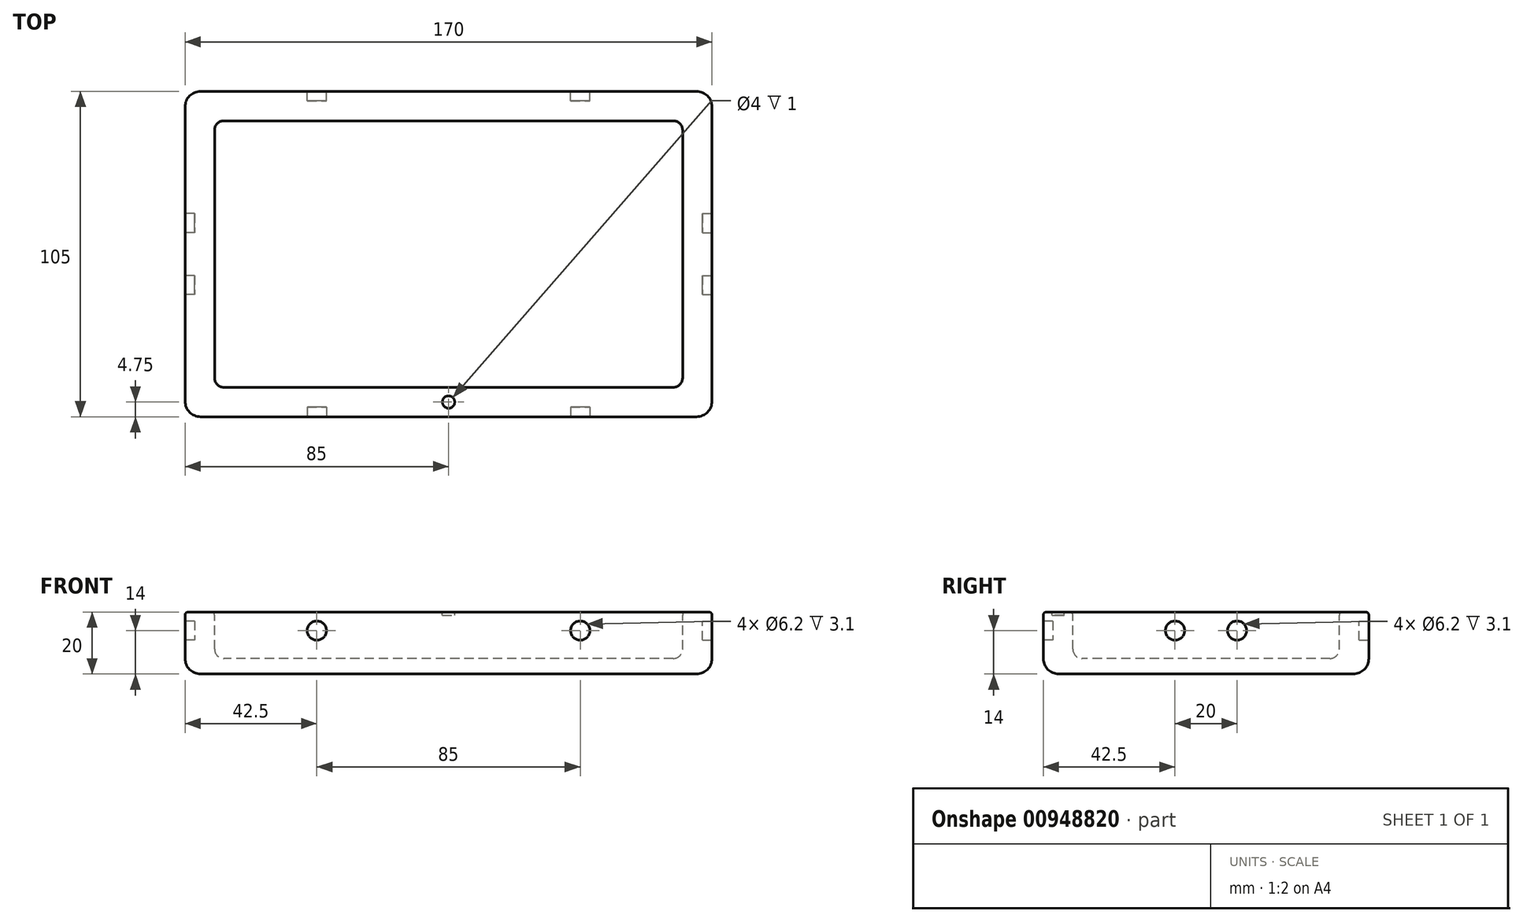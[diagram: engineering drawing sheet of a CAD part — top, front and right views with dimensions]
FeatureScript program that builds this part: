
annotation { "Feature Type Name" : "Feature", "Feature Type Description" : "" }
export const myFeature = defineFeature(function(context is Context, id is Id, definition is map)
    precondition{}
    {
        {
            var Q0;
            Q0=qCreatedBy(makeId("Top.planeOp"),FACE);
            var sketch = newSketch(context, id + "F0", { "sketchPlane" : qUnion([Q0])});
            skLineSegment(sketch, "E0.bottom", {"start": v(-85, 52.5) * mm, "end": v(85, 52.5) * mm});
            skLineSegment(sketch, "E0.top", {"start": v(-85, -52.5) * mm, "end": v(85, -52.5) * mm});
            skLineSegment(sketch, "E0.left", {"start": v(-85, 52.5) * mm, "end": v(-85, -52.5) * mm});
            skLineSegment(sketch, "E0.right", {"start": v(85, 52.5) * mm, "end": v(85, -52.5) * mm});
            skLineSegment(sketch, "E1.bottom", {"start": v(-72.5, 43) * mm, "end": v(72.5, 43) * mm});
            skLineSegment(sketch, "E1.top", {"start": v(-72.5, -43) * mm, "end": v(72.5, -43) * mm});
            skLineSegment(sketch, "E1.left", {"start": v(-75.5, 40) * mm, "end": v(-75.5, -40) * mm});
            skLineSegment(sketch, "E1.right", {"start": v(75.5, 40) * mm, "end": v(75.5, -40) * mm});
            skLineSegment(sketch, "E2.direction1", {"start": v(-75.5, -43) * mm, "end": v(15.26, -43) * mm, "construction": true});
            skPoint(sketch, "E3.visualSharp", {"position": v(-75.5, 43) * mm});
            skArc(sketch, "E3.filletArc", {"start": v(-72.5, 43) * mm, "mid": v(-74.62, 42.12) * mm, "end": v(-75.5, 40) * mm});
            skPoint(sketch, "E4.visualSharp", {"position": v(75.5, 43) * mm});
            skArc(sketch, "E4.filletArc", {"start": v(75.5, 40) * mm, "mid": v(74.62, 42.12) * mm, "end": v(72.5, 43) * mm});
            skPoint(sketch, "E5.visualSharp", {"position": v(75.5, -43) * mm});
            skArc(sketch, "E5.filletArc", {"start": v(72.5, -43) * mm, "mid": v(74.62, -42.12) * mm, "end": v(75.5, -40) * mm});
            skPoint(sketch, "E6.visualSharp", {"position": v(-75.5, -43) * mm});
            skArc(sketch, "E6.filletArc", {"start": v(-75.5, -40) * mm, "mid": v(-74.62, -42.12) * mm, "end": v(-72.5, -43) * mm});
            skLineSegment(sketch, "E7.direction1", {"start": v(-75.5, -43) * mm, "end": v(17, -43) * mm, "construction": true});
            skLineSegment(sketch, "E8", {"start": v(-85, 0) * mm, "end": v(85, 0) * mm, "construction": true});
            skLineSegment(sketch, "E9", {"start": v(0, -52.5) * mm, "end": v(0, 52.5) * mm, "construction": true});
            skCircle(sketch, "E10", {"center": v(0, -47.75) * mm, "radius": 2 * mm});
            skSolve(sketch);
        }
        {
            var Q0;
            Q0=makeQuery(id+"F0.imprint","IMPRINT",FACE,{"disambiguationData":[TD([[makeQuery(id+"F0.imprint","IMPRINT",EDGE,{"derivedFrom":sQuery(id+"F0.wireOp",EDGE,"E1.bottom")}),-1.0]])]});
            var Q1;
            Q1=makeQuery(id+"F0.imprint","IMPRINT",FACE,{"disambiguationData":[TD([[makeQuery(id+"F0.imprint","IMPRINT",EDGE,{"derivedFrom":sQuery(id+"F0.wireOp",EDGE,"E0.bottom")}),-1.0]])]});
            var Q2;
            Q2=makeQuery(id+"F0.imprint","IMPRINT",FACE,{"disambiguationData":[TD([[makeQuery(id+"F0.imprint","IMPRINT",EDGE,{"derivedFrom":sQuery(id+"F0.wireOp",EDGE,"E2.0.2.0")}),1.0]])]});
            var Q3;
            Q3=makeQuery(id+"F0.imprint","IMPRINT",FACE,{"disambiguationData":[TD([[makeQuery(id+"F0.imprint","IMPRINT",EDGE,{"derivedFrom":sQuery(id+"F0.wireOp",EDGE,"E2.0.3.0")}),1.0]])]});
            var Q4;
            Q4=makeQuery(id+"F0.imprint","IMPRINT",FACE,{"disambiguationData":[TD([[makeQuery(id+"F0.imprint","IMPRINT",EDGE,{"derivedFrom":sQuery(id+"F0.wireOp",EDGE,"E2.0.1.0")}),1.0]])]});
            var Q5;
            Q5=makeQuery(id+"F0.imprint","IMPRINT",FACE,{"disambiguationData":[TD([[makeQuery(id+"F0.imprint","IMPRINT",EDGE,{"derivedFrom":sQuery(id+"F0.wireOp",EDGE,"E7.0.1.2")}),1.0]])]});
            var Q6;
            Q6=makeQuery(id+"F0.imprint","IMPRINT",FACE,{"disambiguationData":[TD([[makeQuery(id+"F0.imprint","IMPRINT",EDGE,{"derivedFrom":sQuery(id+"F0.wireOp",EDGE,"E7.0.2.2")}),1.0]])]});
            var Q7;
            Q7=makeQuery(id+"F0.imprint","IMPRINT",FACE,{"disambiguationData":[TD([[makeQuery(id+"F0.imprint","IMPRINT",EDGE,{"derivedFrom":sQuery(id+"F0.wireOp",EDGE,"E7.0.3.2")}),1.0]])]});
            var Q8;
            Q8=makeQuery(id+"F0.imprint","IMPRINT",FACE,{"disambiguationData":[TD([[makeQuery(id+"F0.imprint","IMPRINT",EDGE,{"derivedFrom":sQuery(id+"F0.wireOp",EDGE,"E10")}),1.0]])]});
            extrude(context, id + "F1", {"entities" : qUnion([Q0, Q1, Q2, Q3, Q4, Q5, Q6, Q7, Q8]), "depth" : 20 * mm, "offsetDistance" : 25 * mm});
        }
        {
            var Q0;
            Q0=makeQuery(id+"F0.imprint","IMPRINT",FACE,{"disambiguationData":[TD([[makeQuery(id+"F0.imprint","IMPRINT",EDGE,{"derivedFrom":sQuery(id+"F0.wireOp",EDGE,"E1.bottom")}),-1.0]])]});
            var Q1;
            Q1=makeQuery(id+"F0.imprint","IMPRINT",FACE,{"disambiguationData":[TD([[makeQuery(id+"F0.imprint","IMPRINT",EDGE,{"derivedFrom":sQuery(id+"F0.wireOp",EDGE,"E2.0.1.0")}),1.0]])]});
            var Q2;
            Q2=makeQuery(id+"F0.imprint","IMPRINT",FACE,{"disambiguationData":[TD([[makeQuery(id+"F0.imprint","IMPRINT",EDGE,{"derivedFrom":sQuery(id+"F0.wireOp",EDGE,"E2.0.2.0")}),1.0]])]});
            var Q3;
            Q3=makeQuery(id+"F0.imprint","IMPRINT",FACE,{"disambiguationData":[TD([[makeQuery(id+"F0.imprint","IMPRINT",EDGE,{"derivedFrom":sQuery(id+"F0.wireOp",EDGE,"E2.0.3.0")}),1.0]])]});
            var Q4;
            Q4=makeQuery(id+"F0.imprint","IMPRINT",FACE,{"disambiguationData":[TD([[makeQuery(id+"F0.imprint","IMPRINT",EDGE,{"derivedFrom":sQuery(id+"F0.wireOp",EDGE,"E7.0.1.2")}),1.0]])]});
            var Q5;
            Q5=makeQuery(id+"F0.imprint","IMPRINT",FACE,{"disambiguationData":[TD([[makeQuery(id+"F0.imprint","IMPRINT",EDGE,{"derivedFrom":sQuery(id+"F0.wireOp",EDGE,"E7.0.2.2")}),1.0]])]});
            var Q6;
            Q6=makeQuery(id+"F0.imprint","IMPRINT",FACE,{"disambiguationData":[TD([[makeQuery(id+"F0.imprint","IMPRINT",EDGE,{"derivedFrom":sQuery(id+"F0.wireOp",EDGE,"E7.0.3.2")}),1.0]])]});
            extrude(context, id + "F2", {"entities" : qUnion([Q0, Q1, Q2, Q3, Q4, Q5, Q6]), "operationType" : NewBodyOperationType.REMOVE, "depth" : 15 * mm, "offsetDistance" : 25 * mm});
        }
        {
            var Q0;
            Q0=makeQuery(id+"F1.opExtrude","CAP_FACE",FACE,{"disambiguationData":[OSD([sQuery(id+"F0.wireOp",EDGE,"E0.bottom"),sQuery(id+"F0.wireOp",EDGE,"E0.top"),sQuery(id+"F0.wireOp",EDGE,"E0.left"),sQuery(id+"F0.wireOp",EDGE,"E0.right")])],"isStart":false});
            var Q1;
            Q1=makeQuery(id+"F1.opExtrude","SWEPT_EDGE",EDGE,{"disambiguationData":[OSD([sQuery(id+"F0.wireOp",EDGE,"E0.bottom"),sQuery(id+"F0.wireOp",EDGE,"E0.right")])]});
            var Q2;
            Q2=makeQuery(id+"F1.opExtrude","SWEPT_EDGE",EDGE,{"disambiguationData":[OSD([sQuery(id+"F0.wireOp",EDGE,"E0.bottom"),sQuery(id+"F0.wireOp",EDGE,"E0.left")])]});
            var Q3;
            Q3=makeQuery(id+"F1.opExtrude","SWEPT_EDGE",EDGE,{"disambiguationData":[OSD([sQuery(id+"F0.wireOp",EDGE,"E0.top"),sQuery(id+"F0.wireOp",EDGE,"E0.left")])]});
            var Q4;
            Q4=makeQuery(id+"F1.opExtrude","SWEPT_EDGE",EDGE,{"disambiguationData":[OSD([sQuery(id+"F0.wireOp",EDGE,"E0.top"),sQuery(id+"F0.wireOp",EDGE,"E0.right")])]});
            fillet(context, id + "F3", {"entities" : qUnion([Q0, Q1, Q2, Q3, Q4]), "radius" : 5 * mm, "tangentPropagation" : true, "allowEdgeOverflow" : false});
        }
        {
            var Q0;
            Q0=makeQuery(id+"F2.boolean.opBoolean","COPY",FACE,{"derivedFrom":makeQuery(id+"F2.opExtrude","CAP_FACE",FACE,{"disambiguationData":[OSD([sQuery(id+"F0.wireOp",EDGE,"E1.bottom"),sQuery(id+"F0.wireOp",EDGE,"E1.top"),sQuery(id+"F0.wireOp",EDGE,"E1.left"),sQuery(id+"F0.wireOp",EDGE,"E1.right"),sQuery(id+"F0.wireOp",EDGE,"E3.filletArc"),sQuery(id+"F0.wireOp",EDGE,"E4.filletArc"),sQuery(id+"F0.wireOp",EDGE,"E5.filletArc"),sQuery(id+"F0.wireOp",EDGE,"E6.filletArc")])],"isStart":false})});
            var Q1;
            Q1=makeQuery(id+"F2.boolean.opBoolean","COPY",FACE,{"derivedFrom":makeQuery(id+"F2.opExtrude","CAP_FACE",FACE,{"disambiguationData":[OSD([sQuery(id+"F0.wireOp",EDGE,"E7.0.1.2"),sQuery(id+"F0.wireOp",EDGE,"E7.0.1.4"),sQuery(id+"F0.wireOp",EDGE,"E7.0.1.5"),sQuery(id+"F0.wireOp",EDGE,"E7.0.1.6"),sQuery(id+"F0.wireOp",EDGE,"E7.0.1.7"),sQuery(id+"F0.wireOp",EDGE,"E7.0.1.9"),sQuery(id+"F0.wireOp",EDGE,"E7.0.1.11"),sQuery(id+"F0.wireOp",EDGE,"E7.0.1.12")])],"isStart":false})});
            var Q2;
            Q2=makeQuery(id+"F2.boolean.opBoolean","COPY",FACE,{"derivedFrom":makeQuery(id+"F2.opExtrude","CAP_FACE",FACE,{"disambiguationData":[OSD([sQuery(id+"F0.wireOp",EDGE,"E7.0.2.2"),sQuery(id+"F0.wireOp",EDGE,"E7.0.2.4"),sQuery(id+"F0.wireOp",EDGE,"E7.0.2.5"),sQuery(id+"F0.wireOp",EDGE,"E7.0.2.6"),sQuery(id+"F0.wireOp",EDGE,"E7.0.2.7"),sQuery(id+"F0.wireOp",EDGE,"E7.0.2.9"),sQuery(id+"F0.wireOp",EDGE,"E7.0.2.11"),sQuery(id+"F0.wireOp",EDGE,"E7.0.2.12")])],"isStart":false})});
            var Q3;
            Q3=makeQuery(id+"F2.boolean.opBoolean","COPY",FACE,{"derivedFrom":makeQuery(id+"F2.opExtrude","CAP_FACE",FACE,{"disambiguationData":[OSD([sQuery(id+"F0.wireOp",EDGE,"E7.0.3.2"),sQuery(id+"F0.wireOp",EDGE,"E7.0.3.4"),sQuery(id+"F0.wireOp",EDGE,"E7.0.3.5"),sQuery(id+"F0.wireOp",EDGE,"E7.0.3.6"),sQuery(id+"F0.wireOp",EDGE,"E7.0.3.7"),sQuery(id+"F0.wireOp",EDGE,"E7.0.3.9"),sQuery(id+"F0.wireOp",EDGE,"E7.0.3.11"),sQuery(id+"F0.wireOp",EDGE,"E7.0.3.12")])],"isStart":false})});
            fillet(context, id + "F4", {"entities" : qUnion([Q0, Q1, Q2, Q3]), "radius" : 3 * mm, "tangentPropagation" : true, "allowEdgeOverflow" : false});
        }
        {
            var Q0;
            Q0=makeQuery(id+"F1.opExtrude","CAP_FACE",FACE,{"disambiguationData":[OSD([sQuery(id+"F0.wireOp",EDGE,"E0.bottom"),sQuery(id+"F0.wireOp",EDGE,"E0.top"),sQuery(id+"F0.wireOp",EDGE,"E0.left"),sQuery(id+"F0.wireOp",EDGE,"E0.right")])],"isStart":true});
            fillet(context, id + "F5", {"entities" : qUnion([Q0]), "radius" : 1 * mm, "tangentPropagation" : true, "allowEdgeOverflow" : false});
        }
        {
            var Q0;
            Q0=makeQuery(id+"F1.opExtrude","SWEPT_FACE",FACE,{"disambiguationData":[OSD([sQuery(id+"F0.wireOp",EDGE,"E0.top")])]});
            var sketch = newSketch(context, id + "F6", { "sketchPlane" : qUnion([Q0])});
            skCircle(sketch, "E11", {"center": v(42.5, 6) * mm, "radius": 3.1 * mm});
            skCircle(sketch, "E12", {"center": v(-42.5, 6) * mm, "radius": 3.1 * mm});
            skSolve(sketch);
        }
        {
            var Q0;
            Q0=makeQuery(id+"F6.imprint","IMPRINT",FACE,{"disambiguationData":[TD([[makeQuery(id+"F6.imprint","IMPRINT",EDGE,{"derivedFrom":sQuery(id+"F6.wireOp",EDGE,"E11")}),1.0]])]});
            var Q1;
            Q1=makeQuery(id+"F6.imprint","IMPRINT",FACE,{"disambiguationData":[TD([[makeQuery(id+"F6.imprint","IMPRINT",EDGE,{"derivedFrom":sQuery(id+"F6.wireOp",EDGE,"E12")}),1.0]])]});
            extrude(context, id + "F7", {"entities" : qUnion([Q0, Q1]), "operationType" : NewBodyOperationType.REMOVE, "oppositeDirection" : true, "depth" : 3.1 * mm, "offsetDistance" : 25 * mm});
        }
        {
            var Q0;
            Q0=makeQuery(id+"F1.opExtrude","SWEPT_FACE",FACE,{"disambiguationData":[OSD([sQuery(id+"F0.wireOp",EDGE,"E0.bottom")])]});
            var sketch = newSketch(context, id + "F8", { "sketchPlane" : qUnion([Q0])});
            skCircle(sketch, "E13", {"center": v(42.5, 6) * mm, "radius": 3.1 * mm});
            skCircle(sketch, "E14", {"center": v(-42.5, 6) * mm, "radius": 3.1 * mm});
            skSolve(sketch);
        }
        {
            var Q0;
            Q0=makeQuery(id+"F8.imprint","IMPRINT",FACE,{"disambiguationData":[TD([[makeQuery(id+"F8.imprint","IMPRINT",EDGE,{"derivedFrom":sQuery(id+"F8.wireOp",EDGE,"E13")}),1.0]])]});
            var Q1;
            Q1=makeQuery(id+"F8.imprint","IMPRINT",FACE,{"disambiguationData":[TD([[makeQuery(id+"F8.imprint","IMPRINT",EDGE,{"derivedFrom":sQuery(id+"F8.wireOp",EDGE,"E14")}),1.0]])]});
            extrude(context, id + "F9", {"entities" : qUnion([Q0, Q1]), "operationType" : NewBodyOperationType.REMOVE, "oppositeDirection" : true, "depth" : 3.1 * mm, "offsetDistance" : 25 * mm});
        }
        {
            var Q0;
            Q0=makeQuery(id+"F1.opExtrude","SWEPT_FACE",FACE,{"disambiguationData":[OSD([sQuery(id+"F0.wireOp",EDGE,"E0.left")])]});
            var sketch = newSketch(context, id + "F10", { "sketchPlane" : qUnion([Q0])});
            skCircle(sketch, "E15", {"center": v(10, 6) * mm, "radius": 3.1 * mm});
            skCircle(sketch, "E16", {"center": v(-10, 6) * mm, "radius": 3.1 * mm});
            skSolve(sketch);
        }
        {
            var Q0;
            Q0=makeQuery(id+"F10.imprint","IMPRINT",FACE,{"disambiguationData":[TD([[makeQuery(id+"F10.imprint","IMPRINT",EDGE,{"derivedFrom":sQuery(id+"F10.wireOp",EDGE,"E15")}),1.0]])]});
            var Q1;
            Q1=makeQuery(id+"F10.imprint","IMPRINT",FACE,{"disambiguationData":[TD([[makeQuery(id+"F10.imprint","IMPRINT",EDGE,{"derivedFrom":sQuery(id+"F10.wireOp",EDGE,"E16")}),1.0]])]});
            extrude(context, id + "F11", {"entities" : qUnion([Q0, Q1]), "operationType" : NewBodyOperationType.REMOVE, "oppositeDirection" : true, "depth" : 3.1 * mm, "offsetDistance" : 25 * mm});
        }
        {
            var Q0;
            Q0=makeQuery(id+"F1.opExtrude","SWEPT_FACE",FACE,{"disambiguationData":[OSD([sQuery(id+"F0.wireOp",EDGE,"E0.right")])]});
            var sketch = newSketch(context, id + "F12", { "sketchPlane" : qUnion([Q0])});
            skCircle(sketch, "E17", {"center": v(10, 6) * mm, "radius": 3.1 * mm});
            skCircle(sketch, "E18", {"center": v(-10, 6) * mm, "radius": 3.1 * mm});
            skSolve(sketch);
        }
        {
            var Q0;
            Q0=makeQuery(id+"F12.imprint","IMPRINT",FACE,{"disambiguationData":[TD([[makeQuery(id+"F12.imprint","IMPRINT",EDGE,{"derivedFrom":sQuery(id+"F12.wireOp",EDGE,"E17")}),1.0]])]});
            var Q1;
            Q1=makeQuery(id+"F12.imprint","IMPRINT",FACE,{"disambiguationData":[TD([[makeQuery(id+"F12.imprint","IMPRINT",EDGE,{"derivedFrom":sQuery(id+"F12.wireOp",EDGE,"E18")}),1.0]])]});
            extrude(context, id + "F13", {"entities" : qUnion([Q0, Q1]), "operationType" : NewBodyOperationType.REMOVE, "oppositeDirection" : true, "depth" : 3.1 * mm, "offsetDistance" : 25 * mm});
        }
        {
            var Q0;
            Q0=makeQuery(id+"F0.imprint","IMPRINT",FACE,{"disambiguationData":[TD([[makeQuery(id+"F0.imprint","IMPRINT",EDGE,{"derivedFrom":sQuery(id+"F0.wireOp",EDGE,"E10")}),1.0]])]});
            var Q1;
            Q1=sQuery(id+"F0.wireOp",EDGE,"E10");
            extrude(context, id + "F14", {"entities" : qUnion([Q0]), "operationType" : NewBodyOperationType.REMOVE, "surfaceEntities" : qUnion([Q1]), "depth" : 1 * mm, "offsetDistance" : 25 * mm});
        }
        {
            var Q0;
            Q0=makeQuery(id+"F1.opExtrude","SWEPT_BODY",BODY,{"disambiguationData":[OSD([sQuery(id+"F0.wireOp",EDGE,"E0.bottom"),sQuery(id+"F0.wireOp",EDGE,"E0.top"),sQuery(id+"F0.wireOp",EDGE,"E0.left"),sQuery(id+"F0.wireOp",EDGE,"E0.right")])]});
            var Q1;
            Q1=sQuery(id+"F0.wireOp",EDGE,"E9");
            transform(context, id + "F15", {"entities" : qUnion([Q0]), "transformType" : TransformType.ROTATION, "transformAxis" : qUnion([Q1]), "angle" : 180 * degree, "makeCopy" : false});
        }
    });
